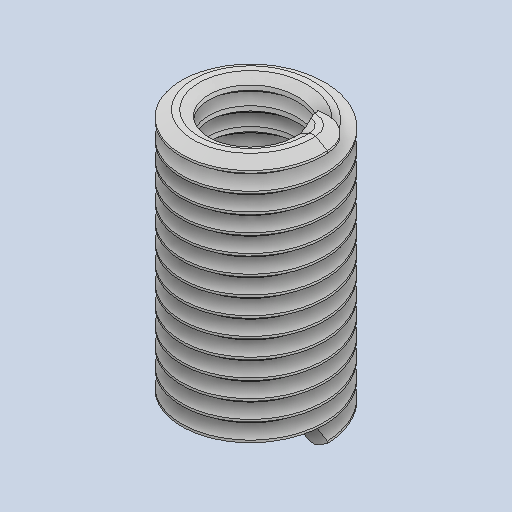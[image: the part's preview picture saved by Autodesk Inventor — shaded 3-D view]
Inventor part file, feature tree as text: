
AUTODESK INVENTOR PART (.ipt)
format: ipt  version: 2022 (Build 260153000, 153)  size: 630,272 bytes
history: native  units: in
note: dims shown in document units (in); Inventor stores cm internally (conversion verified against a paired STEP export)
features: sweep x1, other x1
ambient origin geometry x8: Origin, YZ Plane, XZ Plane, XY Plane, X Axis, Y Axis, Z Axis, Center Point
bodies: Solid1 (feature_tree), Solid2 (feature_tree)
feature tree (2):
  sweep  "Sweep1"
  other  "Cut-Extrude1"
